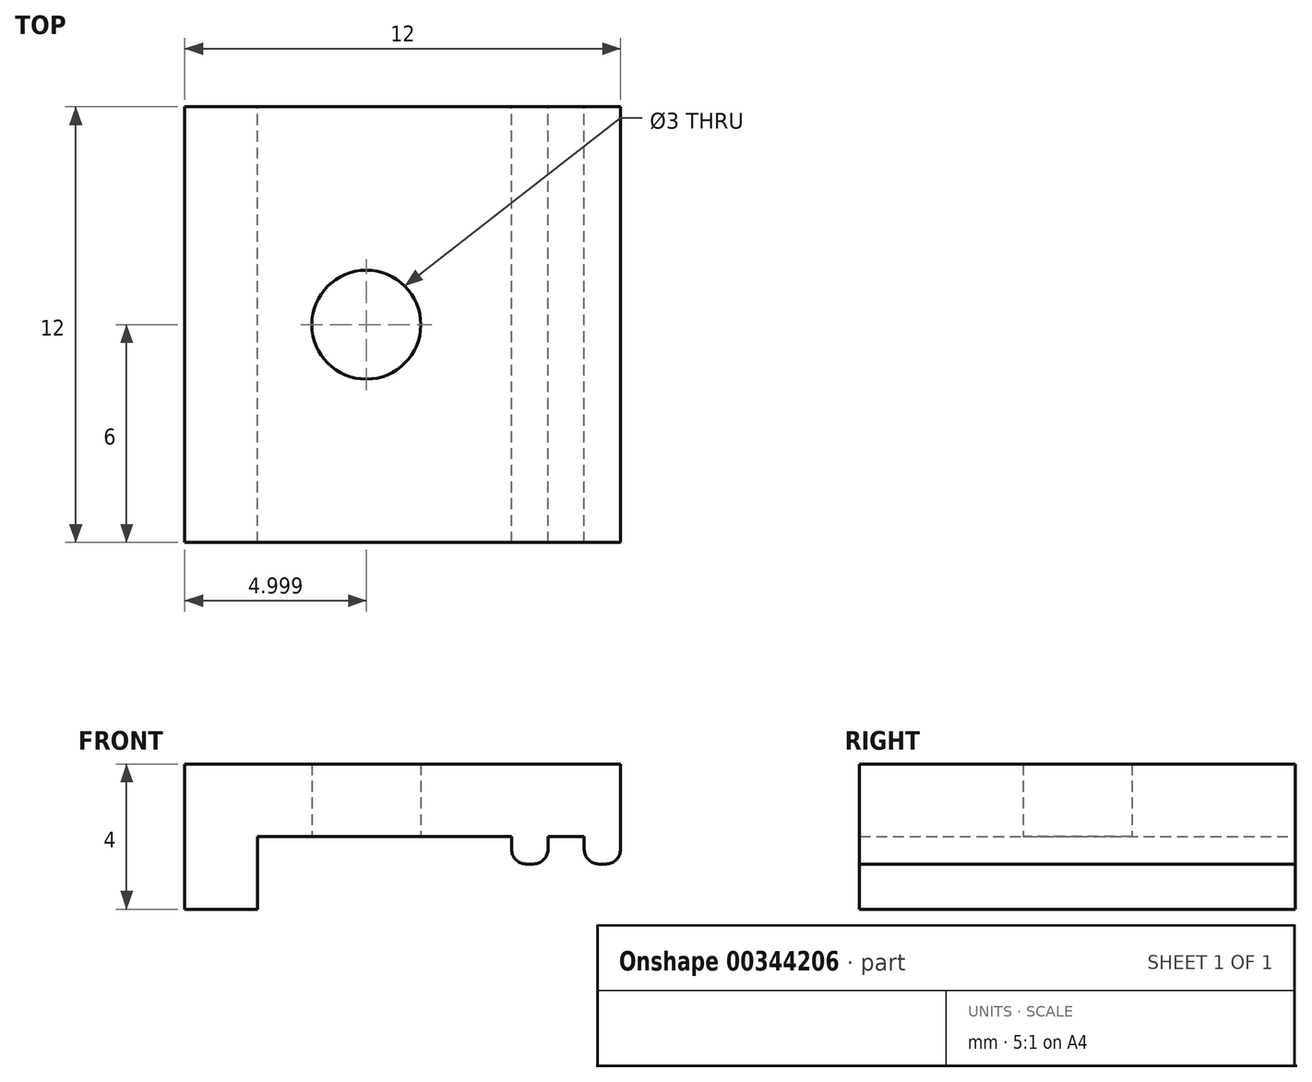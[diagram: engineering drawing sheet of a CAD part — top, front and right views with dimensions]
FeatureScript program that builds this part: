
annotation { "Feature Type Name" : "Feature", "Feature Type Description" : "" }
export const myFeature = defineFeature(function(context is Context, id is Id, definition is map)
    precondition{}
    {
        {
            var Q0;
            Q0=qCreatedBy(makeId("Front.planeOp"),FACE);
            var sketch = newSketch(context, id + "F0", { "sketchPlane" : qUnion([Q0])});
            skLineSegment(sketch, "E0.bottom", {"start": v(19.3, 6.9) * mm, "end": v(31.3, 6.9) * mm});
            skLineSegment(sketch, "E0.top", {"start": v(19.3, 2.9) * mm, "end": v(21.3, 2.9) * mm});
            skLineSegment(sketch, "E0.left", {"start": v(19.3, 6.9) * mm, "end": v(19.3, 2.9) * mm});
            skLineSegment(sketch, "E0.right", {"start": v(31.3, 6.9) * mm, "end": v(31.3, 4.56) * mm});
            skLineSegment(sketch, "E1.top", {"start": v(21.3, 4.9) * mm, "end": v(28.3, 4.9) * mm});
            skLineSegment(sketch, "E1.left", {"start": v(21.3, 2.9) * mm, "end": v(21.3, 4.9) * mm});
            skLineSegment(sketch, "E2.top", {"start": v(28.7, 4.16) * mm, "end": v(28.9, 4.16) * mm});
            skLineSegment(sketch, "E3.left", {"start": v(31.3, 5.32) * mm, "end": v(31.3, 5.4) * mm});
            skLineSegment(sketch, "E4.trimOffspring", {"start": v(28.3, 4.56) * mm, "end": v(28.3, 4.9) * mm});
            skLineSegment(sketch, "E5.top", {"start": v(30.3, 4.9) * mm, "end": v(29.3, 4.9) * mm});
            skLineSegment(sketch, "E5.left", {"start": v(30.3, 4.56) * mm, "end": v(30.3, 4.9) * mm});
            skLineSegment(sketch, "E5.right", {"start": v(29.3, 4.56) * mm, "end": v(29.3, 4.9) * mm});
            skLineSegment(sketch, "E6.trimOffspring", {"start": v(30.7, 4.16) * mm, "end": v(30.9, 4.16) * mm});
            skPoint(sketch, "E7.visualSharp", {"position": v(31.3, 4.16) * mm});
            skArc(sketch, "E7.filletArc", {"start": v(30.9, 4.16) * mm, "mid": v(31.2, 4.27) * mm, "end": v(31.3, 4.56) * mm});
            skPoint(sketch, "E8.visualSharp", {"position": v(30.3, 4.16) * mm});
            skArc(sketch, "E8.filletArc", {"start": v(30.3, 4.56) * mm, "mid": v(30.43, 4.27) * mm, "end": v(30.7, 4.16) * mm});
            skPoint(sketch, "E9.visualSharp", {"position": v(29.3, 4.16) * mm});
            skArc(sketch, "E9.filletArc", {"start": v(28.9, 4.16) * mm, "mid": v(29.2, 4.27) * mm, "end": v(29.3, 4.56) * mm});
            skPoint(sketch, "E10.visualSharp", {"position": v(28.3, 4.16) * mm});
            skArc(sketch, "E10.filletArc", {"start": v(28.3, 4.56) * mm, "mid": v(28.43, 4.27) * mm, "end": v(28.7, 4.16) * mm});
            skSolve(sketch);
        }
        {
            var Q0;
            Q0 = qSketchRegion(id + "F0", true);
            extrude(context, id + "F1", {"entities" : qUnion([Q0]), "depth" : 12 * mm});
        }
        {
            var Q0;
            Q0=makeQuery(id+"F1.opExtrude","SWEPT_FACE",FACE,{"disambiguationData":[OSD([sQuery(id+"F0.wireOp",EDGE,"E1.top")])]});
            var sketch = newSketch(context, id + "F2", { "sketchPlane" : qUnion([Q0])});
            skLineSegment(sketch, "E11", {"start": v(21.3, 6) * mm, "end": v(26.93, 6) * mm, "construction": true});
            skCircle(sketch, "E12", {"center": v(24.3, 6) * mm, "radius": 1.5 * mm});
            skSolve(sketch);
        }
        {
            var Q0;
            Q0 = qSketchRegion(id + "F2", true);
            extrude(context, id + "F3", {"entities" : qUnion([Q0]), "operationType" : NewBodyOperationType.REMOVE, "oppositeDirection" : true, "depth" : 25 * mm});
        }
    });
